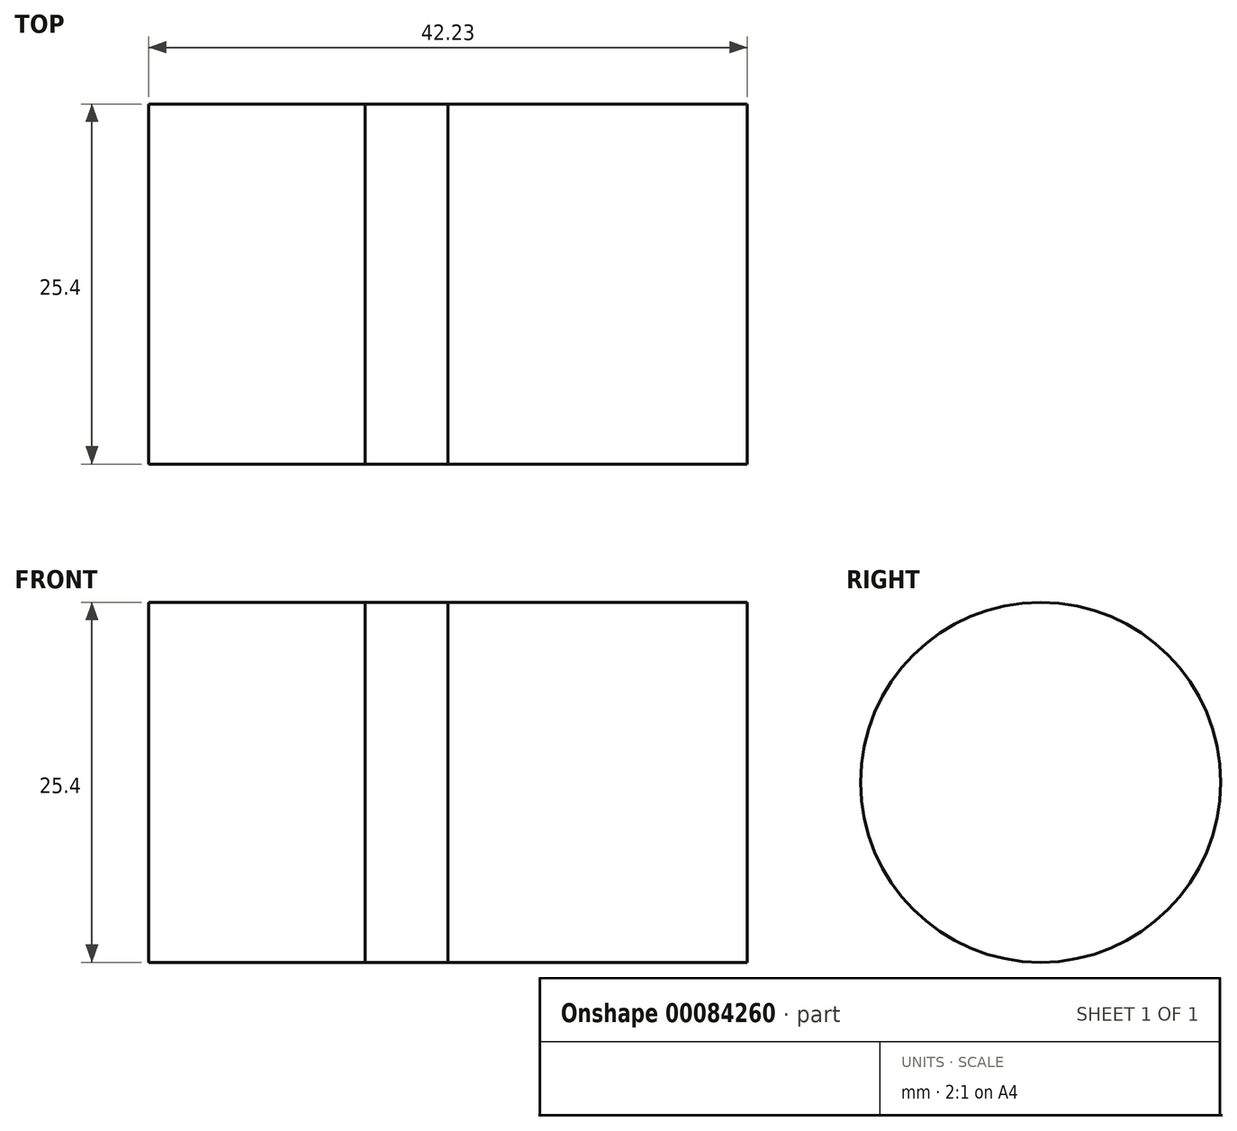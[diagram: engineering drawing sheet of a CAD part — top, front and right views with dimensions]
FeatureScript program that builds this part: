
annotation { "Feature Type Name" : "Feature", "Feature Type Description" : "" }
export const myFeature = defineFeature(function(context is Context, id is Id, definition is map)
    precondition{}
    {
        {
            var Q0;
            Q0=qCreatedBy(makeId("Front.planeOp"),FACE);
            var sketch = newSketch(context, id + "F0", { "sketchPlane" : qUnion([Q0])});
            skLineSegment(sketch, "E0", {"start": v(0, 0) * mm, "end": v(0, 12.7) * mm});
            skLineSegment(sketch, "E1", {"start": v(0, 12.7) * mm, "end": v(10.16, 12.7) * mm});
            skLineSegment(sketch, "E2", {"start": v(10.16, 12.7) * mm, "end": v(10.16, 10.16) * mm});
            skLineSegment(sketch, "E3", {"start": v(10.16, 10.16) * mm, "end": v(56.13, 10.16) * mm});
            skLineSegment(sketch, "E4", {"start": v(56.13, 10.16) * mm, "end": v(56.13, 12.7) * mm});
            skLineSegment(sketch, "E5", {"start": v(56.13, 12.7) * mm, "end": v(66.3, 12.7) * mm});
            skLineSegment(sketch, "E6", {"start": v(66.3, 12.7) * mm, "end": v(66.3, 0) * mm});
            skLineSegment(sketch, "E7", {"start": v(66.3, 0) * mm, "end": v(0, 0) * mm});
            skLineSegment(sketch, "E8", {"start": v(5.84, 15.24) * mm, "end": v(-0.5, 15.24) * mm});
            skLineSegment(sketch, "E9", {"start": v(-0.5, 15.24) * mm, "end": v(-10.88, 3.85) * mm});
            skLineSegment(sketch, "E10", {"start": v(0, 0) * mm, "end": v(-6.65, 0) * mm});
            skCircle(sketch, "E11", {"center": v(-6.65, 0) * mm, "radius": 5.72 * mm});
            skCircle(sketch, "E12", {"center": v(-6.65, 0) * mm, "radius": 3.18 * mm});
            skLineSegment(sketch, "E13", {"start": v(5.84, 15.24) * mm, "end": v(5.84, -9.4) * mm});
            skLineSegment(sketch, "E14", {"start": v(5.84, -9.4) * mm, "end": v(-8.18, -5.5) * mm});
            skSolve(sketch);
        }
        {
            var Q0;
            {var subQ0=sQuery(id+"F0.wireOp",EDGE,"E0");Q0=makeQuery(id+"F0.imprint","IMPRINT",FACE,{"disambiguationData":[TD([[makeQuery(id+"F0.imprint","IMPRINT",EDGE,{"derivedFrom":subQ0}),-1.0]])]});}
            var Q1;
            Q1=sQuery(id+"F0.wireOp",EDGE,"E7");
            revolve(context, id + "F1", {"entities" : qUnion([Q0]), "axis" : qUnion([Q1]), "revolveType" : RevolveType.FULL});
        }
        {
            var Q0;
            Q0=makeQuery(id+"F1.opRevolve","SWEPT_FACE",FACE,{"disambiguationData":[OSD([sQuery(id+"F0.wireOp",EDGE,"E13")])]});
            extrude(context, id + "F2", {"entities" : qUnion([Q0]), "endBound" : BoundingType.SYMMETRIC, "depth" : 42.23 * mm});
        }
    });
